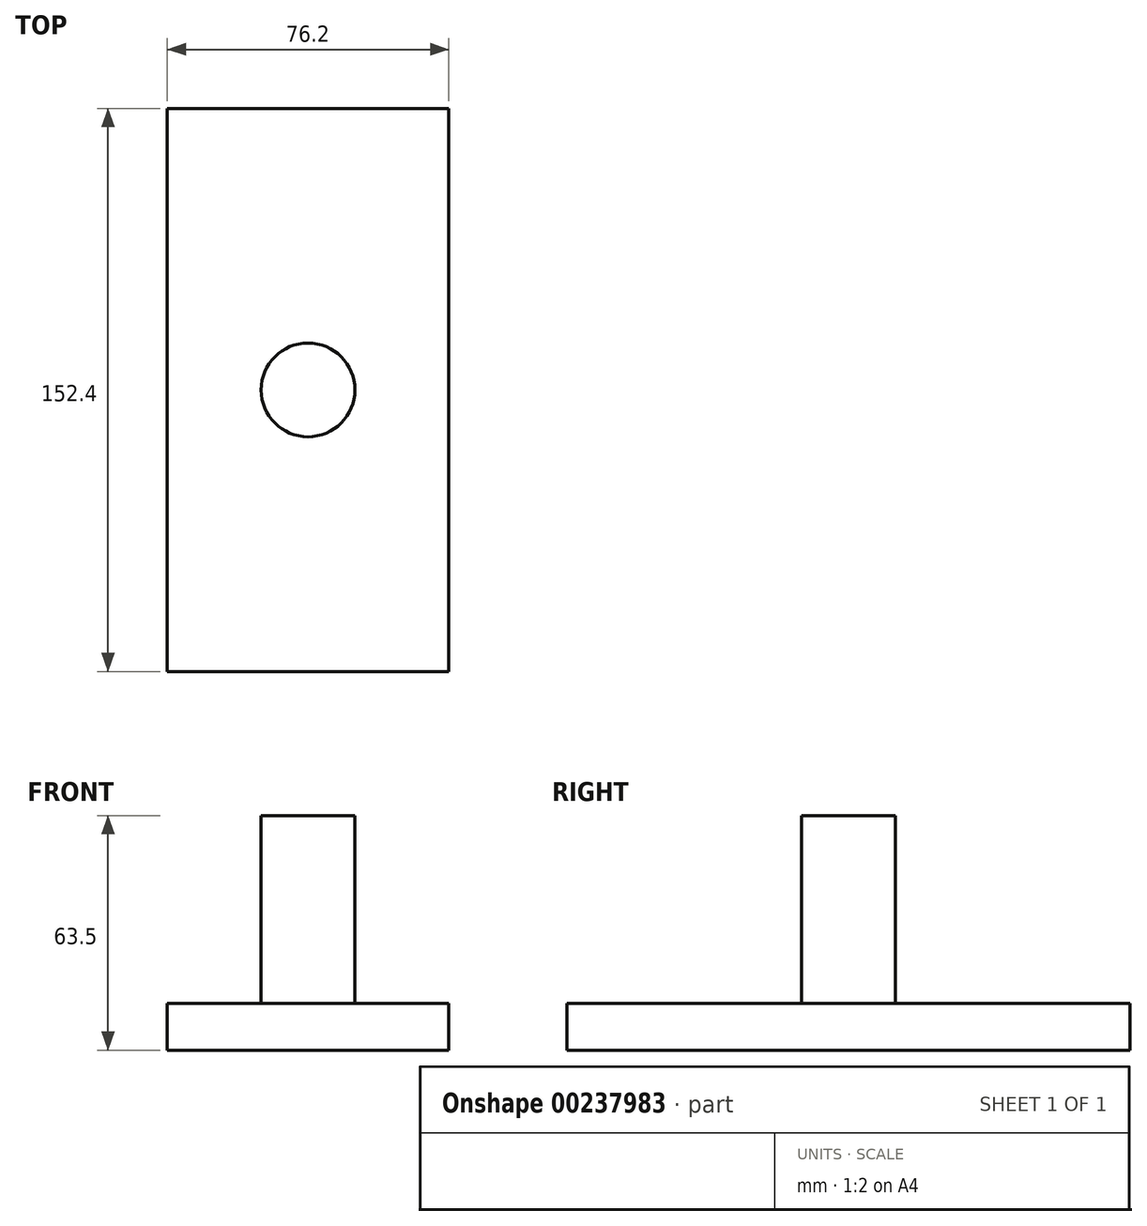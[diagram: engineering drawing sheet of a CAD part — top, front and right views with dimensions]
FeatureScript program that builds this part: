
annotation { "Feature Type Name" : "Feature", "Feature Type Description" : "" }
export const myFeature = defineFeature(function(context is Context, id is Id, definition is map)
    precondition{}
    {
        {
            var Q0;
            Q0=qCreatedBy(makeId("Top.planeOp"),FACE);
            var sketch = newSketch(context, id + "F0", { "sketchPlane" : qUnion([Q0])});
            skCircle(sketch, "E0", {"center": v(0, 0) * mm, "radius": 12.7 * mm});
            skSolve(sketch);
        }
        {
            var Q0;
            Q0 = qSketchRegion(id + "F0", true);
            extrude(context, id + "F1", {"entities" : qUnion([Q0]), "depth" : 50.8 * mm});
        }
        {
            var Q0;
            Q0=qCreatedBy(makeId("Top.planeOp"),FACE);
            var sketch = newSketch(context, id + "F2", { "sketchPlane" : qUnion([Q0])});
            skLineSegment(sketch, "E1.bottom", {"start": v(38.1, -76.2) * mm, "end": v(-38.1, -76.2) * mm});
            skLineSegment(sketch, "E1.top", {"start": v(38.1, 76.2) * mm, "end": v(-38.1, 76.2) * mm});
            skLineSegment(sketch, "E1.left", {"start": v(38.1, -76.2) * mm, "end": v(38.1, 76.2) * mm});
            skLineSegment(sketch, "E1.right", {"start": v(-38.1, -76.2) * mm, "end": v(-38.1, 76.2) * mm});
            skPoint(sketch, "E1.middle", {"position": v(0, 0) * mm});
            skSolve(sketch);
        }
        {
            var Q0;
            Q0 = qSketchRegion(id + "F2", true);
            extrude(context, id + "F3", {"entities" : qUnion([Q0]), "operationType" : NewBodyOperationType.ADD, "oppositeDirection" : true, "depth" : 12.7 * mm});
        }
    });
